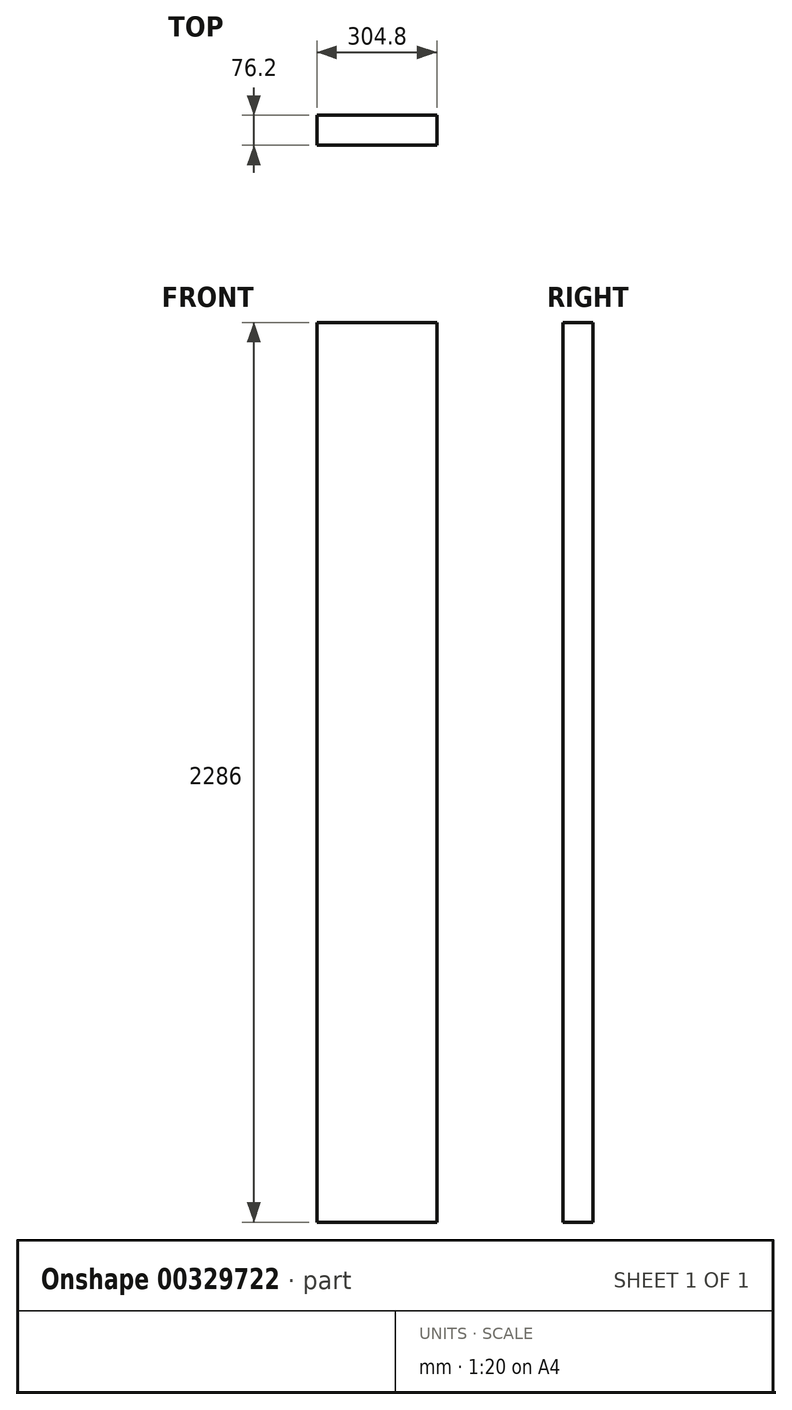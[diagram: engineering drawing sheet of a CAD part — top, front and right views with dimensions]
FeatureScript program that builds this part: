
annotation { "Feature Type Name" : "Feature", "Feature Type Description" : "" }
export const myFeature = defineFeature(function(context is Context, id is Id, definition is map)
    precondition{}
    {
        {
            var Q0;
            Q0=qCreatedBy(makeId("Front.planeOp"),FACE);
            var sketch = newSketch(context, id + "F0", { "sketchPlane" : qUnion([Q0])});
            skLineSegment(sketch, "E0.bottom", {"start": v(-152.4, 1143) * mm, "end": v(152.4, 1143) * mm});
            skLineSegment(sketch, "E0.top", {"start": v(-152.4, -1143) * mm, "end": v(152.4, -1143) * mm});
            skLineSegment(sketch, "E0.left", {"start": v(-152.4, 1143) * mm, "end": v(-152.4, -1143) * mm});
            skLineSegment(sketch, "E0.right", {"start": v(152.4, 1143) * mm, "end": v(152.4, -1143) * mm});
            skPoint(sketch, "E0.middle", {"position": v(0, 0) * mm});
            skSolve(sketch);
        }
        {
            var Q0;
            Q0=makeQuery(id+"F0.imprint","IMPRINT",FACE,{"disambiguationData":[TD([[makeQuery(id+"F0.imprint","IMPRINT",EDGE,{"derivedFrom":sQuery(id+"F0.wireOp",EDGE,"E0.bottom")}),-1.0]])]});
            extrude(context, id + "F1", {"entities" : qUnion([Q0]), "endBound" : BoundingType.SYMMETRIC, "depth" : 76.2 * mm});
        }
    });
